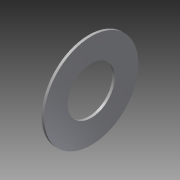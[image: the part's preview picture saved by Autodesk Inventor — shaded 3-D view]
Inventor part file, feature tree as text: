
AUTODESK INVENTOR PART (.ipt)
format: ipt  version: 2014 SP1 (Build 180222100, 222)  size: 77,824 bytes
history: native  units: in
note: dims shown in document units (in); Inventor stores cm internally (conversion verified against a paired STEP export)
features: extrude x1, sketch x1
ambient origin geometry x8: Origin, YZ Plane, XZ Plane, XY Plane, X Axis, Y Axis, Z Axis, Center Point
bodies: Solid1 (feature_tree)
feature tree (2):
  extrude  "Extrusion1"  Depth=0.0197in
  sketch  "Sketch1"  dims[d0=0.375in d1=0.75in d2=0.0197in d3=0.0in]
